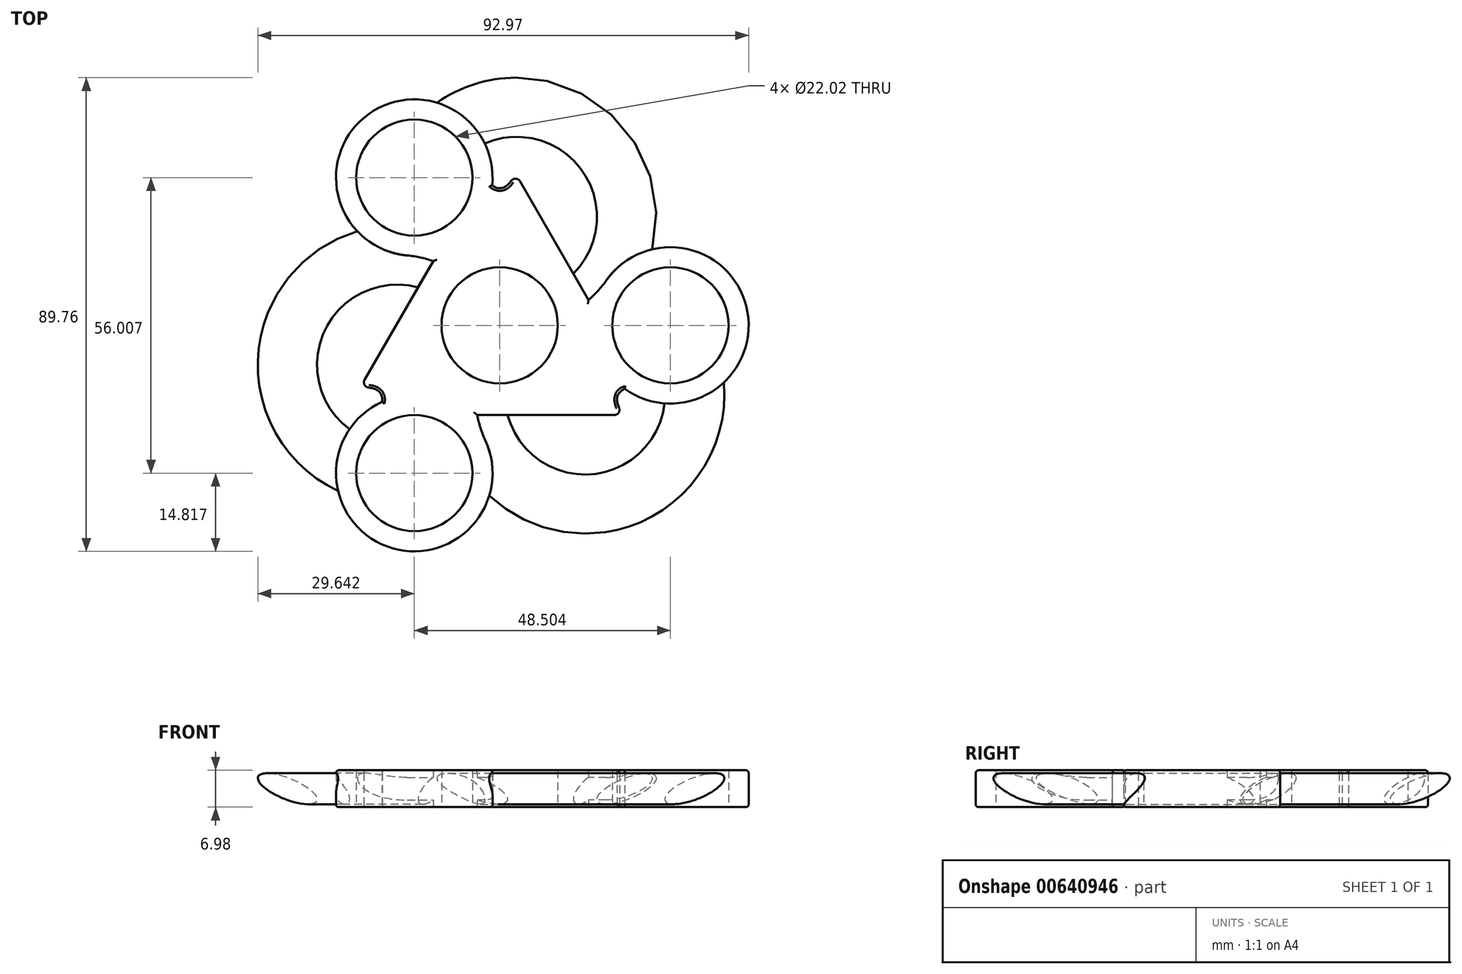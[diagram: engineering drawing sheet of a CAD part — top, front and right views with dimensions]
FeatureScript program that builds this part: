
annotation { "Feature Type Name" : "Feature", "Feature Type Description" : "" }
export const myFeature = defineFeature(function(context is Context, id is Id, definition is map)
    precondition{}
    {
        {
            var Q0;
            Q0=qCreatedBy(makeId("Top.planeOp"),FACE);
            var sketch = newSketch(context, id + "F0", { "sketchPlane" : qUnion([Q0])});
            skCircle(sketch, "E0", {"center": v(0, 0) * mm, "radius": 11.01 * mm});
            skArc(sketch, "E1", {"start": v(0, 0) * mm, "mid": v(21.25, 30.94) * mm, "end": v(-16.17, 28) * mm});
            skArc(sketch, "E2", {"start": v(0, 0) * mm, "mid": v(-37.42, 2.93) * mm, "end": v(-16.17, -28) * mm});
            skArc(sketch, "E3", {"start": v(0, 0) * mm, "mid": v(16.17, -33.87) * mm, "end": v(32.34, 0) * mm});
            skPoint(sketch, "E4", {"position": v(-16.17, 28) * mm});
            skPoint(sketch, "E5", {"position": v(-16.17, -28) * mm});
            skPoint(sketch, "E6", {"position": v(32.34, 0) * mm});
            skCircle(sketch, "E7", {"center": v(-16.17, 28) * mm, "radius": 11.01 * mm});
            skCircle(sketch, "E8", {"center": v(-16.17, -28) * mm, "radius": 11.01 * mm});
            skCircle(sketch, "E9", {"center": v(32.34, 0) * mm, "radius": 11.01 * mm});
            skPoint(sketch, "E10.start.orphan", {"position": v(52.35, 0) * mm});
            skLineSegment(sketch, "E11.0", {"start": v(2.97, 28.85) * mm, "end": v(26.47, -11.86) * mm});
            skLineSegment(sketch, "E11.1", {"start": v(-26.47, -11.86) * mm, "end": v(-2.97, 28.85) * mm});
            skLineSegment(sketch, "E11.2", {"start": v(23.5, -17) * mm, "end": v(-23.5, -17) * mm});
            skEllipticalArc(sketch, "E12", {});
            skEllipticalArc(sketch, "E13", {});
            skEllipticalArc(sketch, "E14", {});
            skLineSegment(sketch, "E15", {"start": v(0, 0) * mm, "end": v(32.34, 0) * mm});
            skLineSegment(sketch, "E16", {"start": v(0, 0) * mm, "end": v(-16.17, 28) * mm});
            skLineSegment(sketch, "E17", {"start": v(0, 0) * mm, "end": v(-16.17, -28) * mm});
            skLineSegment(sketch, "E18", {"start": v(0, 0) * mm, "end": v(26.47, -11.86) * mm});
            skLineSegment(sketch, "E19", {"start": v(0, 0) * mm, "end": v(23.5, -17) * mm});
            skLineSegment(sketch, "E20", {"start": v(0, 0) * mm, "end": v(-23.5, -17) * mm});
            skLineSegment(sketch, "E21", {"start": v(0, 0) * mm, "end": v(-26.47, -11.86) * mm});
            skLineSegment(sketch, "E22", {"start": v(0, 0) * mm, "end": v(2.97, 28.85) * mm});
            skLineSegment(sketch, "E23", {"start": v(0, 0) * mm, "end": v(-2.97, 28.85) * mm});
            skCircle(sketch, "E24", {"center": v(32.34, 0) * mm, "radius": 14.82 * mm});
            skCircle(sketch, "E25", {"center": v(-16.17, -28) * mm, "radius": 14.82 * mm});
            skCircle(sketch, "E26", {"center": v(-16.17, 28) * mm, "radius": 14.82 * mm});
            const initialGuessF0  = {"E12": [0, 0.033985290935932826, 0, -1, 0.008, 0.00386931025616376, 5.409716549895262, 0.8734687572843228], "E13": [0.029432125305522916, -0.01699264546796644, 0.8660254037844404, -0.5, 0.008, 0.0038693102561636484, 2.2681238963054615, 4.015061410874123], "E14": [-0.02943212530552289, -0.01699264546796644, -0.8660254037844388, -0.5, 0.008, 0.003869310256163598, 2.2681238963054624, 4.015061410874123]};
            skSetInitialGuess(sketch, initialGuessF0);
            skSolve(sketch);
        }
        {
            var Q0;
            Q0=sQuery(id+"F0.wireOp",VERTEX,"E1.end");
            var Q1;
            Q1=sQuery(id+"F0.wireOp",EDGE,"E1");
            cPlane(context, id + "F1", {"entities" : qUnion([Q0, Q1]), "cplaneType" : CPlaneType.CURVE_POINT, "offset" : 25 * mm, "width" : 150 * mm, "height" : 150 * mm});
        }
        {
            var Q0;
            Q0=sQuery(id+"F0.wireOp",VERTEX,"E2.end");
            var Q1;
            Q1=sQuery(id+"F0.wireOp",EDGE,"E2");
            cPlane(context, id + "F2", {"entities" : qUnion([Q0, Q1]), "cplaneType" : CPlaneType.CURVE_POINT, "offset" : 25 * mm, "width" : 150 * mm, "height" : 150 * mm});
        }
        {
            var Q0;
            Q0=sQuery(id+"F0.wireOp",VERTEX,"E3.end");
            var Q1;
            Q1=sQuery(id+"F0.wireOp",EDGE,"E3");
            cPlane(context, id + "F3", {"entities" : qUnion([Q0, Q1]), "cplaneType" : CPlaneType.CURVE_POINT, "offset" : 25 * mm, "width" : 150 * mm, "height" : 150 * mm});
        }
        {
            var Q0;
            Q0=qCreatedBy(id+"F1.planeOp",FACE);
            var sketch = newSketch(context, id + "F4", { "sketchPlane" : qUnion([Q0])});
            skEllipse(sketch, "E27", {"center": v(-25.14, 0) * mm, "majorRadius": 6 * mm, "minorRadius": 2 * mm, "majorAxis": v(-0.93, 0.38)});
            skSolve(sketch);
        }
        {
            var Q0;
            Q0=qCreatedBy(id+"F2.planeOp",FACE);
            var sketch = newSketch(context, id + "F5", { "sketchPlane" : qUnion([Q0])});
            skEllipse(sketch, "E28", {"center": v(-25.14, 0) * mm, "majorRadius": 6 * mm, "minorRadius": 2 * mm, "majorAxis": v(-0.93, 0.38)});
            skSolve(sketch);
        }
        {
            var Q0;
            Q0=qCreatedBy(id+"F3.planeOp",FACE);
            var sketch = newSketch(context, id + "F6", { "sketchPlane" : qUnion([Q0])});
            skEllipse(sketch, "E29", {"center": v(-25.14, 0) * mm, "majorRadius": 6 * mm, "minorRadius": 2 * mm, "majorAxis": v(-0.93, 0.38)});
            skSolve(sketch);
        }
        {
            var Q0;
            Q0=makeQuery(id+"F5.imprint","IMPRINT",FACE,{"disambiguationData":[TD([[makeQuery(id+"F5.imprint","IMPRINT",EDGE,{"derivedFrom":sQuery(id+"F5.wireOp",EDGE,"E28")}),1.0]])]});
            var Q1;
            Q1=sQuery(id+"F0.wireOp",EDGE,"E2");
            sweep(context, id + "F7", {"profiles" : qUnion([Q0]), "path" : qUnion([Q1])});
        }
        {
            var Q0;
            Q0=makeQuery(id+"F4.imprint","IMPRINT",FACE,{"disambiguationData":[TD([[makeQuery(id+"F4.imprint","IMPRINT",EDGE,{"derivedFrom":sQuery(id+"F4.wireOp",EDGE,"E27")}),1.0]])]});
            var Q1;
            Q1=sQuery(id+"F0.wireOp",EDGE,"E1");
            sweep(context, id + "F8", {"operationType" : NewBodyOperationType.ADD, "profiles" : qUnion([Q0]), "path" : qUnion([Q1])});
        }
        {
            var Q0;
            Q0=makeQuery(id+"F6.imprint","IMPRINT",FACE,{"disambiguationData":[TD([[makeQuery(id+"F6.imprint","IMPRINT",EDGE,{"derivedFrom":sQuery(id+"F6.wireOp",EDGE,"E29")}),1.0]])]});
            var Q1;
            Q1=sQuery(id+"F0.wireOp",EDGE,"E3");
            sweep(context, id + "F9", {"operationType" : NewBodyOperationType.ADD, "profiles" : qUnion([Q0]), "path" : qUnion([Q1])});
        }
        {
            var Q0;
            {var subQ0=sQuery(id+"F0.wireOp",EDGE,"E24");var subQ1=sQuery(id+"F0.wireOp",EDGE,"E1");var subQ2=makeQuery(id+"F0.imprint","INTERSECT",VERTEX,{"derivedFrom":[subQ1,subQ0]});Q0=makeQuery(id+"F0.imprint","IMPRINT",FACE,{"disambiguationData":[TD([[makeQuery(id+"F0.imprint","IMPRINT",EDGE,{"disambiguationData":[TD([[subQ2,1.0]])],"derivedFrom":subQ1}),-1.0]])]});}
            var Q1;
            {var subQ0=sQuery(id+"F0.wireOp",EDGE,"E26");var subQ1=sQuery(id+"F0.wireOp",EDGE,"E2");var subQ2=makeQuery(id+"F0.imprint","INTERSECT",VERTEX,{"derivedFrom":[subQ1,subQ0]});Q1=makeQuery(id+"F0.imprint","IMPRINT",FACE,{"disambiguationData":[TD([[makeQuery(id+"F0.imprint","IMPRINT",EDGE,{"disambiguationData":[TD([[subQ2,1.0]])],"derivedFrom":subQ1}),-1.0]])]});}
            var Q2;
            {var subQ0=sQuery(id+"F0.wireOp",EDGE,"E25");var subQ1=sQuery(id+"F0.wireOp",EDGE,"E3");var subQ2=makeQuery(id+"F0.imprint","INTERSECT",VERTEX,{"derivedFrom":[subQ1,subQ0]});Q2=makeQuery(id+"F0.imprint","IMPRINT",FACE,{"disambiguationData":[TD([[makeQuery(id+"F0.imprint","IMPRINT",EDGE,{"disambiguationData":[TD([[subQ2,1.0]])],"derivedFrom":subQ1}),-1.0]])]});}
            var Q3;
            {var subQ0=sQuery(id+"F0.wireOp",EDGE,"E26");var subQ7=sQuery(id+"F0.wireOp",EDGE,"E1");var subQ9=makeQuery(id+"F0.imprint","INTERSECT",VERTEX,{"derivedFrom":[subQ7,subQ0]});Q3=makeQuery(id+"F0.imprint","IMPRINT",FACE,{"disambiguationData":[TD([[makeQuery(id+"F0.imprint","IMPRINT",EDGE,{"disambiguationData":[TD([[subQ9,-1.0]])],"derivedFrom":subQ7}),-1.0]])]});}
            var Q4;
            {var subQ5=sQuery(id+"F0.wireOp",EDGE,"E1");var subQ7=sQuery(id+"F0.wireOp",EDGE,"E26");var subQ9=makeQuery(id+"F0.imprint","INTERSECT",VERTEX,{"derivedFrom":[subQ5,subQ7]});Q4=makeQuery(id+"F0.imprint","IMPRINT",FACE,{"disambiguationData":[TD([[makeQuery(id+"F0.imprint","IMPRINT",EDGE,{"disambiguationData":[TD([[subQ9,-1.0]])],"derivedFrom":subQ5}),1.0]])]});}
            var Q5;
            {var subQ3=sQuery(id+"F0.wireOp",EDGE,"E25");var subQ7=sQuery(id+"F0.wireOp",EDGE,"E2");var subQ9=makeQuery(id+"F0.imprint","INTERSECT",VERTEX,{"derivedFrom":[subQ7,subQ3]});Q5=makeQuery(id+"F0.imprint","IMPRINT",FACE,{"disambiguationData":[TD([[makeQuery(id+"F0.imprint","IMPRINT",EDGE,{"disambiguationData":[TD([[subQ9,-1.0]])],"derivedFrom":subQ7}),1.0]])]});}
            var Q6;
            {var subQ3=sQuery(id+"F0.wireOp",EDGE,"E24");var subQ6=sQuery(id+"F0.wireOp",EDGE,"E3");var subQ9=makeQuery(id+"F0.imprint","INTERSECT",VERTEX,{"derivedFrom":[subQ6,subQ3]});Q6=makeQuery(id+"F0.imprint","IMPRINT",FACE,{"disambiguationData":[TD([[makeQuery(id+"F0.imprint","IMPRINT",EDGE,{"disambiguationData":[TD([[subQ9,-1.0]])],"derivedFrom":subQ6}),1.0]])]});}
            var Q7;
            {var subQ5=sQuery(id+"F0.wireOp",EDGE,"E24");var subQ7=sQuery(id+"F0.wireOp",EDGE,"E3");var subQ10=makeQuery(id+"F0.imprint","INTERSECT",VERTEX,{"derivedFrom":[subQ7,subQ5]});Q7=makeQuery(id+"F0.imprint","IMPRINT",FACE,{"disambiguationData":[TD([[makeQuery(id+"F0.imprint","IMPRINT",EDGE,{"disambiguationData":[TD([[subQ10,-1.0]])],"derivedFrom":subQ7}),-1.0]])]});}
            var Q8;
            {var subQ1=sQuery(id+"F0.wireOp",EDGE,"E0");var subQ5=sQuery(id+"F0.wireOp",EDGE,"E19");var subQ9=makeQuery(id+"F0.imprint","INTERSECT",VERTEX,{"derivedFrom":[subQ1,subQ5]});Q8=makeQuery(id+"F0.imprint","IMPRINT",FACE,{"disambiguationData":[TD([[makeQuery(id+"F0.imprint","IMPRINT",EDGE,{"disambiguationData":[TD([[subQ9,-1.0]])],"derivedFrom":subQ1}),-1.0]])]});}
            var Q9;
            {var subQ0=sQuery(id+"F0.wireOp",EDGE,"E15");var subQ1=sQuery(id+"F0.wireOp",EDGE,"E0");var subQ2=makeQuery(id+"F0.imprint","INTERSECT",VERTEX,{"derivedFrom":[subQ1,subQ0]});Q9=makeQuery(id+"F0.imprint","IMPRINT",FACE,{"disambiguationData":[TD([[makeQuery(id+"F0.imprint","IMPRINT",EDGE,{"disambiguationData":[TD([[subQ2,1.0]])],"derivedFrom":subQ1}),-1.0]])]});}
            var Q10;
            {var subQ1=sQuery(id+"F0.wireOp",EDGE,"E1");var subQ6=sQuery(id+"F0.wireOp",EDGE,"E0");var subQ9=makeQuery(id+"F0.imprint","INTERSECT",VERTEX,{"derivedFrom":[subQ6,subQ1]});Q10=makeQuery(id+"F0.imprint","IMPRINT",FACE,{"disambiguationData":[TD([[makeQuery(id+"F0.imprint","IMPRINT",EDGE,{"disambiguationData":[TD([[subQ9,1.0]])],"derivedFrom":subQ6}),-1.0]])]});}
            var Q11;
            {var subQ0=sQuery(id+"F0.wireOp",EDGE,"E1");var subQ1=sQuery(id+"F0.wireOp",EDGE,"E0");var subQ2=makeQuery(id+"F0.imprint","INTERSECT",VERTEX,{"derivedFrom":[subQ1,subQ0]});Q11=makeQuery(id+"F0.imprint","IMPRINT",FACE,{"disambiguationData":[TD([[makeQuery(id+"F0.imprint","IMPRINT",EDGE,{"disambiguationData":[TD([[subQ2,-1.0]])],"derivedFrom":subQ1}),-1.0]])]});}
            var Q12;
            {var subQ0=sQuery(id+"F0.wireOp",EDGE,"E26");var subQ1=sQuery(id+"F0.wireOp",EDGE,"E11.1");var subQ2=makeQuery(id+"F0.imprint","INTERSECT",VERTEX,{"derivedFrom":[subQ1,subQ0]});Q12=makeQuery(id+"F0.imprint","IMPRINT",FACE,{"disambiguationData":[TD([[makeQuery(id+"F0.imprint","IMPRINT",EDGE,{"disambiguationData":[TD([[subQ2,-1.0]])],"derivedFrom":subQ1}),-1.0]])]});}
            var Q13;
            {var subQ1=sQuery(id+"F0.wireOp",EDGE,"E11.1");var subQ5=makeQuery(id+"F0.imprint","INTERSECT",VERTEX,{"derivedFrom":[sQuery(id+"F0.wireOp",EDGE,"E7"),subQ1]});Q13=makeQuery(id+"F0.imprint","IMPRINT",FACE,{"disambiguationData":[TD([[makeQuery(id+"F0.imprint","IMPRINT",EDGE,{"disambiguationData":[TD([[subQ5,1.0]])],"derivedFrom":subQ1}),-1.0]])]});}
            var Q14;
            {var subQ5=sQuery(id+"F0.wireOp",EDGE,"E16");var subQ6=sQuery(id+"F0.wireOp",EDGE,"E0");var subQ7=makeQuery(id+"F0.imprint","INTERSECT",VERTEX,{"derivedFrom":[subQ6,subQ5]});Q14=makeQuery(id+"F0.imprint","IMPRINT",FACE,{"disambiguationData":[TD([[makeQuery(id+"F0.imprint","IMPRINT",EDGE,{"disambiguationData":[TD([[subQ7,-1.0]])],"derivedFrom":subQ6}),-1.0]])]});}
            var Q15;
            {var subQ0=sQuery(id+"F0.wireOp",EDGE,"E2");var subQ1=sQuery(id+"F0.wireOp",EDGE,"E0");var subQ2=makeQuery(id+"F0.imprint","INTERSECT",VERTEX,{"derivedFrom":[subQ1,subQ0]});Q15=makeQuery(id+"F0.imprint","IMPRINT",FACE,{"disambiguationData":[TD([[makeQuery(id+"F0.imprint","IMPRINT",EDGE,{"disambiguationData":[TD([[subQ2,-1.0]])],"derivedFrom":subQ1}),-1.0]])]});}
            var Q16;
            {var subQ0=sQuery(id+"F0.wireOp",EDGE,"E21");var subQ3=sQuery(id+"F0.wireOp",EDGE,"E0");var subQ4=makeQuery(id+"F0.imprint","INTERSECT",VERTEX,{"derivedFrom":[subQ3,subQ0]});Q16=makeQuery(id+"F0.imprint","IMPRINT",FACE,{"disambiguationData":[TD([[makeQuery(id+"F0.imprint","IMPRINT",EDGE,{"disambiguationData":[TD([[subQ4,-1.0]])],"derivedFrom":subQ3}),-1.0]])]});}
            var Q17;
            {var subQ0=sQuery(id+"F0.wireOp",EDGE,"E20");var subQ1=sQuery(id+"F0.wireOp",EDGE,"E0");var subQ2=makeQuery(id+"F0.imprint","INTERSECT",VERTEX,{"derivedFrom":[subQ1,subQ0]});Q17=makeQuery(id+"F0.imprint","IMPRINT",FACE,{"disambiguationData":[TD([[makeQuery(id+"F0.imprint","IMPRINT",EDGE,{"disambiguationData":[TD([[subQ2,-1.0]])],"derivedFrom":subQ1}),-1.0]])]});}
            var Q18;
            {var subQ0=sQuery(id+"F0.wireOp",EDGE,"E17");var subQ1=sQuery(id+"F0.wireOp",EDGE,"E0");var subQ2=makeQuery(id+"F0.imprint","INTERSECT",VERTEX,{"derivedFrom":[subQ1,subQ0]});Q18=makeQuery(id+"F0.imprint","IMPRINT",FACE,{"disambiguationData":[TD([[makeQuery(id+"F0.imprint","IMPRINT",EDGE,{"disambiguationData":[TD([[subQ2,-1.0]])],"derivedFrom":subQ1}),-1.0]])]});}
            var Q19;
            {var subQ1=sQuery(id+"F0.wireOp",EDGE,"E11.2");var subQ5=makeQuery(id+"F0.imprint","INTERSECT",VERTEX,{"derivedFrom":[sQuery(id+"F0.wireOp",EDGE,"E8"),subQ1]});Q19=makeQuery(id+"F0.imprint","IMPRINT",FACE,{"disambiguationData":[TD([[makeQuery(id+"F0.imprint","IMPRINT",EDGE,{"disambiguationData":[TD([[subQ5,1.0]])],"derivedFrom":subQ1}),-1.0]])]});}
            var Q20;
            {var subQ1=sQuery(id+"F0.wireOp",EDGE,"E14");var subQ3=sQuery(id+"F0.wireOp",EDGE,"E25");var subQ4=makeQuery(id+"F0.imprint","INTERSECT",VERTEX,{"derivedFrom":[subQ1,subQ3]});Q20=makeQuery(id+"F0.imprint","IMPRINT",FACE,{"disambiguationData":[TD([[makeQuery(id+"F0.imprint","IMPRINT",EDGE,{"disambiguationData":[TD([[subQ4,1.0]])],"derivedFrom":subQ3}),1.0]])]});}
            var Q21;
            {var subQ0=sQuery(id+"F0.wireOp",EDGE,"E16");var subQ1=sQuery(id+"F0.wireOp",EDGE,"E7");var subQ2=makeQuery(id+"F0.imprint","INTERSECT",VERTEX,{"derivedFrom":[subQ1,subQ0]});Q21=makeQuery(id+"F0.imprint","IMPRINT",FACE,{"disambiguationData":[TD([[makeQuery(id+"F0.imprint","IMPRINT",EDGE,{"disambiguationData":[TD([[subQ2,-1.0]])],"derivedFrom":subQ1}),-1.0]])]});}
            var Q22;
            {var subQ1=sQuery(id+"F0.wireOp",EDGE,"E12");var subQ3=sQuery(id+"F0.wireOp",EDGE,"E26");var subQ4=makeQuery(id+"F0.imprint","INTERSECT",VERTEX,{"derivedFrom":[subQ1,subQ3]});Q22=makeQuery(id+"F0.imprint","IMPRINT",FACE,{"disambiguationData":[TD([[makeQuery(id+"F0.imprint","IMPRINT",EDGE,{"disambiguationData":[TD([[subQ4,1.0]])],"derivedFrom":subQ3}),1.0]])]});}
            var Q23;
            {var subQ1=sQuery(id+"F0.wireOp",EDGE,"E0");var subQ5=sQuery(id+"F0.wireOp",EDGE,"E22");var subQ9=makeQuery(id+"F0.imprint","INTERSECT",VERTEX,{"derivedFrom":[subQ1,subQ5]});Q23=makeQuery(id+"F0.imprint","IMPRINT",FACE,{"disambiguationData":[TD([[makeQuery(id+"F0.imprint","IMPRINT",EDGE,{"disambiguationData":[TD([[subQ9,-1.0]])],"derivedFrom":subQ1}),-1.0]])]});}
            var Q24;
            {var subQ0=sQuery(id+"F0.wireOp",EDGE,"E23");var subQ1=sQuery(id+"F0.wireOp",EDGE,"E0");var subQ2=makeQuery(id+"F0.imprint","INTERSECT",VERTEX,{"derivedFrom":[subQ1,subQ0]});Q24=makeQuery(id+"F0.imprint","IMPRINT",FACE,{"disambiguationData":[TD([[makeQuery(id+"F0.imprint","IMPRINT",EDGE,{"disambiguationData":[TD([[subQ2,-1.0]])],"derivedFrom":subQ1}),-1.0]])]});}
            var Q25;
            {var subQ1=sQuery(id+"F0.wireOp",EDGE,"E11.0");var subQ8=makeQuery(id+"F0.imprint","INTERSECT",VERTEX,{"derivedFrom":[sQuery(id+"F0.wireOp",EDGE,"E9"),subQ1]});Q25=makeQuery(id+"F0.imprint","IMPRINT",FACE,{"disambiguationData":[TD([[makeQuery(id+"F0.imprint","IMPRINT",EDGE,{"disambiguationData":[TD([[subQ8,1.0]])],"derivedFrom":subQ1}),-1.0]])]});}
            var Q26;
            {var subQ0=sQuery(id+"F0.wireOp",EDGE,"E24");var subQ1=sQuery(id+"F0.wireOp",EDGE,"E11.0");var subQ2=makeQuery(id+"F0.imprint","INTERSECT",VERTEX,{"derivedFrom":[subQ1,subQ0]});Q26=makeQuery(id+"F0.imprint","IMPRINT",FACE,{"disambiguationData":[TD([[makeQuery(id+"F0.imprint","IMPRINT",EDGE,{"disambiguationData":[TD([[subQ2,-1.0]])],"derivedFrom":subQ1}),-1.0]])]});}
            var Q27;
            {var subQ0=sQuery(id+"F0.wireOp",EDGE,"E11.0");var subQ1=sQuery(id+"F0.wireOp",EDGE,"E9");var subQ2=makeQuery(id+"F0.imprint","INTERSECT",VERTEX,{"derivedFrom":[subQ1,subQ0]});Q27=makeQuery(id+"F0.imprint","IMPRINT",FACE,{"disambiguationData":[TD([[makeQuery(id+"F0.imprint","IMPRINT",EDGE,{"disambiguationData":[TD([[subQ2,1.0]])],"derivedFrom":subQ1}),-1.0]])]});}
            var Q28;
            {var subQ1=sQuery(id+"F0.wireOp",EDGE,"E13");var subQ3=sQuery(id+"F0.wireOp",EDGE,"E24");var subQ4=makeQuery(id+"F0.imprint","INTERSECT",VERTEX,{"derivedFrom":[subQ1,subQ3]});Q28=makeQuery(id+"F0.imprint","IMPRINT",FACE,{"disambiguationData":[TD([[makeQuery(id+"F0.imprint","IMPRINT",EDGE,{"disambiguationData":[TD([[subQ4,1.0]])],"derivedFrom":subQ3}),1.0]])]});}
            var Q29;
            {var subQ0=sQuery(id+"F0.wireOp",EDGE,"E11.2");var subQ1=sQuery(id+"F0.wireOp",EDGE,"E8");var subQ2=makeQuery(id+"F0.imprint","INTERSECT",VERTEX,{"derivedFrom":[subQ1,subQ0]});Q29=makeQuery(id+"F0.imprint","IMPRINT",FACE,{"disambiguationData":[TD([[makeQuery(id+"F0.imprint","IMPRINT",EDGE,{"disambiguationData":[TD([[subQ2,1.0]])],"derivedFrom":subQ1}),-1.0]])]});}
            var Q30;
            {var subQ1=sQuery(id+"F0.wireOp",EDGE,"E2");var subQ7=sQuery(id+"F0.wireOp",EDGE,"E25");var subQ8=makeQuery(id+"F0.imprint","INTERSECT",VERTEX,{"derivedFrom":[subQ1,subQ7]});Q30=makeQuery(id+"F0.imprint","IMPRINT",FACE,{"disambiguationData":[TD([[makeQuery(id+"F0.imprint","IMPRINT",EDGE,{"disambiguationData":[TD([[subQ8,-1.0]])],"derivedFrom":subQ1}),-1.0]])]});}
            var Q31;
            {var subQ0=sQuery(id+"F0.wireOp",EDGE,"E25");var subQ1=sQuery(id+"F0.wireOp",EDGE,"E11.2");var subQ2=makeQuery(id+"F0.imprint","INTERSECT",VERTEX,{"derivedFrom":[subQ1,subQ0]});Q31=makeQuery(id+"F0.imprint","IMPRINT",FACE,{"disambiguationData":[TD([[makeQuery(id+"F0.imprint","IMPRINT",EDGE,{"disambiguationData":[TD([[subQ2,-1.0]])],"derivedFrom":subQ1}),-1.0]])]});}
            var Q32;
            {var subQ0=sQuery(id+"F0.wireOp",EDGE,"E3");var subQ1=sQuery(id+"F0.wireOp",EDGE,"E0");var subQ2=makeQuery(id+"F0.imprint","INTERSECT",VERTEX,{"derivedFrom":[subQ1,subQ0]});Q32=makeQuery(id+"F0.imprint","IMPRINT",FACE,{"disambiguationData":[TD([[makeQuery(id+"F0.imprint","IMPRINT",EDGE,{"disambiguationData":[TD([[subQ2,-1.0]])],"derivedFrom":subQ1}),-1.0]])]});}
            extrude(context, id + "F10", {"entities" : qUnion([Q0, Q1, Q2, Q3, Q4, Q5, Q6, Q7, Q8, Q9, Q10, Q11, Q12, Q13, Q14, Q15, Q16, Q17, Q18, Q19, Q20, Q21, Q22, Q23, Q24, Q25, Q26, Q27, Q28, Q29, Q30, Q31, Q32]), "operationType" : NewBodyOperationType.ADD, "endBound" : BoundingType.SYMMETRIC, "depth" : 7 * mm, "offsetDistance" : 25 * mm});
        }
        {
            var Q0;
            Q0=makeQuery(id+"F10.opExtrude","CAP_FACE",FACE,{"disambiguationData":[OSD([sQuery(id+"F0.wireOp",EDGE,"E0"),sQuery(id+"F0.wireOp",EDGE,"E1"),sQuery(id+"F0.wireOp",EDGE,"E2"),sQuery(id+"F0.wireOp",EDGE,"E3"),sQuery(id+"F0.wireOp",EDGE,"E7"),sQuery(id+"F0.wireOp",EDGE,"E8"),sQuery(id+"F0.wireOp",EDGE,"E9"),sQuery(id+"F0.wireOp",EDGE,"E11.0"),sQuery(id+"F0.wireOp",EDGE,"E11.1"),sQuery(id+"F0.wireOp",EDGE,"E11.2"),sQuery(id+"F0.wireOp",EDGE,"E12"),sQuery(id+"F0.wireOp",EDGE,"E13"),sQuery(id+"F0.wireOp",EDGE,"E14"),sQuery(id+"F0.wireOp",EDGE,"E24"),sQuery(id+"F0.wireOp",EDGE,"E25"),sQuery(id+"F0.wireOp",EDGE,"E26")])],"isStart":false});
            var sketch = newSketch(context, id + "F11", { "sketchPlane" : qUnion([Q0])});
            skCircle(sketch, "E30", {"center": v(0, 0) * mm, "radius": 11.01 * mm});
            skLineSegment(sketch, "E31", {"start": v(0, 0) * mm, "end": v(32.34, 0) * mm});
            skCircle(sketch, "E32", {"center": v(32.34, 0) * mm, "radius": 11.01 * mm});
            skLineSegment(sketch, "E33", {"start": v(0, 0) * mm, "end": v(-16.17, 28) * mm});
            skLineSegment(sketch, "E34", {"start": v(0, 0) * mm, "end": v(-16.17, -28) * mm});
            skCircle(sketch, "E35", {"center": v(-16.17, 28) * mm, "radius": 11.01 * mm});
            skCircle(sketch, "E36", {"center": v(-16.17, -28) * mm, "radius": 11.01 * mm});
            skSolve(sketch);
        }
        {
            var Q0;
            Q0 = qSketchRegion(id + "F11", true);
            extrude(context, id + "F12", {"entities" : qUnion([Q0]), "operationType" : NewBodyOperationType.REMOVE, "oppositeDirection" : true, "depth" : 25 * mm, "offsetDistance" : 25 * mm});
        }
        {
            var Q0;
            Q0=makeQuery(id+"F10.opExtrude","CAP_EDGE",EDGE,{"disambiguationData":[OSD([sQuery(id+"F0.wireOp",EDGE,"E26")])],"isStart":false});
            var Q1;
            Q1=makeQuery(id+"F10.opExtrude","CAP_EDGE",EDGE,{"disambiguationData":[OSD([sQuery(id+"F0.wireOp",EDGE,"E11.1")])],"isStart":false});
            var Q2;
            Q2=makeQuery(id+"F10.opExtrude","CAP_EDGE",EDGE,{"disambiguationData":[OSD([sQuery(id+"F0.wireOp",EDGE,"E11.0")])],"isStart":false});
            var Q3;
            Q3=makeQuery(id+"F10.opExtrude","CAP_EDGE",EDGE,{"disambiguationData":[OSD([sQuery(id+"F0.wireOp",EDGE,"E24")])],"isStart":false});
            var Q4;
            Q4=makeQuery(id+"F10.opExtrude","CAP_EDGE",EDGE,{"disambiguationData":[OSD([sQuery(id+"F0.wireOp",EDGE,"E11.2")])],"isStart":false});
            var Q5;
            Q5=makeQuery(id+"F10.opExtrude","CAP_EDGE",EDGE,{"disambiguationData":[OSD([sQuery(id+"F0.wireOp",EDGE,"E25")])],"isStart":false});
            var Q6;
            Q6=makeQuery(id+"F10.opExtrude","CAP_EDGE",EDGE,{"disambiguationData":[OSD([sQuery(id+"F0.wireOp",EDGE,"E14")])],"isStart":false});
            var Q7;
            Q7=makeQuery(id+"F10.opExtrude","CAP_EDGE",EDGE,{"disambiguationData":[OSD([sQuery(id+"F0.wireOp",EDGE,"E12")])],"isStart":false});
            var Q8;
            Q8=makeQuery(id+"F10.opExtrude","CAP_EDGE",EDGE,{"disambiguationData":[OSD([sQuery(id+"F0.wireOp",EDGE,"E13")])],"isStart":false});
            fillet(context, id + "F13", {"entities" : qUnion([Q0, Q1, Q2, Q3, Q4, Q5, Q6, Q7, Q8]), "radius" : .5 * mm, "tangentPropagation" : true, "allowEdgeOverflow" : false});
        }
        {
            var Q0;
            Q0=makeQuery(id+"F10.opExtrude","CAP_EDGE",EDGE,{"disambiguationData":[OSD([sQuery(id+"F0.wireOp",EDGE,"E11.0")])],"isStart":true});
            var Q1;
            Q1=makeQuery(id+"F10.opExtrude","CAP_EDGE",EDGE,{"disambiguationData":[OSD([sQuery(id+"F0.wireOp",EDGE,"E26")])],"isStart":true});
            var Q2;
            Q2=makeQuery(id+"F10.opExtrude","CAP_EDGE",EDGE,{"disambiguationData":[OSD([sQuery(id+"F0.wireOp",EDGE,"E11.1")])],"isStart":true});
            var Q3;
            Q3=makeQuery(id+"F10.opExtrude","CAP_EDGE",EDGE,{"disambiguationData":[OSD([sQuery(id+"F0.wireOp",EDGE,"E11.2")])],"isStart":true});
            var Q4;
            Q4=makeQuery(id+"F10.opExtrude","CAP_EDGE",EDGE,{"disambiguationData":[OSD([sQuery(id+"F0.wireOp",EDGE,"E25")])],"isStart":true});
            var Q5;
            Q5=makeQuery(id+"F10.opExtrude","CAP_EDGE",EDGE,{"disambiguationData":[OSD([sQuery(id+"F0.wireOp",EDGE,"E24")])],"isStart":true});
            var Q6;
            Q6=makeQuery(id+"F10.opExtrude","CAP_EDGE",EDGE,{"disambiguationData":[OSD([sQuery(id+"F0.wireOp",EDGE,"E13")])],"isStart":true});
            var Q7;
            Q7=makeQuery(id+"F10.opExtrude","CAP_EDGE",EDGE,{"disambiguationData":[OSD([sQuery(id+"F0.wireOp",EDGE,"E14")])],"isStart":true});
            var Q8;
            Q8=makeQuery(id+"F10.opExtrude","CAP_EDGE",EDGE,{"disambiguationData":[OSD([sQuery(id+"F0.wireOp",EDGE,"E12")])],"isStart":true});
            fillet(context, id + "F14", {"entities" : qUnion([Q0, Q1, Q2, Q3, Q4, Q5, Q6, Q7, Q8]), "radius" : .5 * mm, "tangentPropagation" : true, "allowEdgeOverflow" : false});
        }
        {
            var Q0;
            Q0=makeQuery(id+"F10.opExtrude","SWEPT_EDGE",EDGE,{"disambiguationData":[OSD([sQuery(id+"F0.wireOp",EDGE,"E11.1"),sQuery(id+"F0.wireOp",EDGE,"E14"),sQuery(id+"F0.wireOp",EDGE,"E21")])]});
            var Q1;
            Q1=makeQuery(id+"F10.opExtrude","SWEPT_EDGE",EDGE,{"disambiguationData":[OSD([sQuery(id+"F0.wireOp",EDGE,"E11.2"),sQuery(id+"F0.wireOp",EDGE,"E13"),sQuery(id+"F0.wireOp",EDGE,"E19")])]});
            var Q2;
            Q2=makeQuery(id+"F10.opExtrude","SWEPT_EDGE",EDGE,{"disambiguationData":[OSD([sQuery(id+"F0.wireOp",EDGE,"E11.0"),sQuery(id+"F0.wireOp",EDGE,"E12"),sQuery(id+"F0.wireOp",EDGE,"E22")])]});
            fillet(context, id + "F15", {"entities" : qUnion([Q0, Q1, Q2]), "radius" : 1 * mm, "tangentPropagation" : true, "allowEdgeOverflow" : false});
        }
    });
